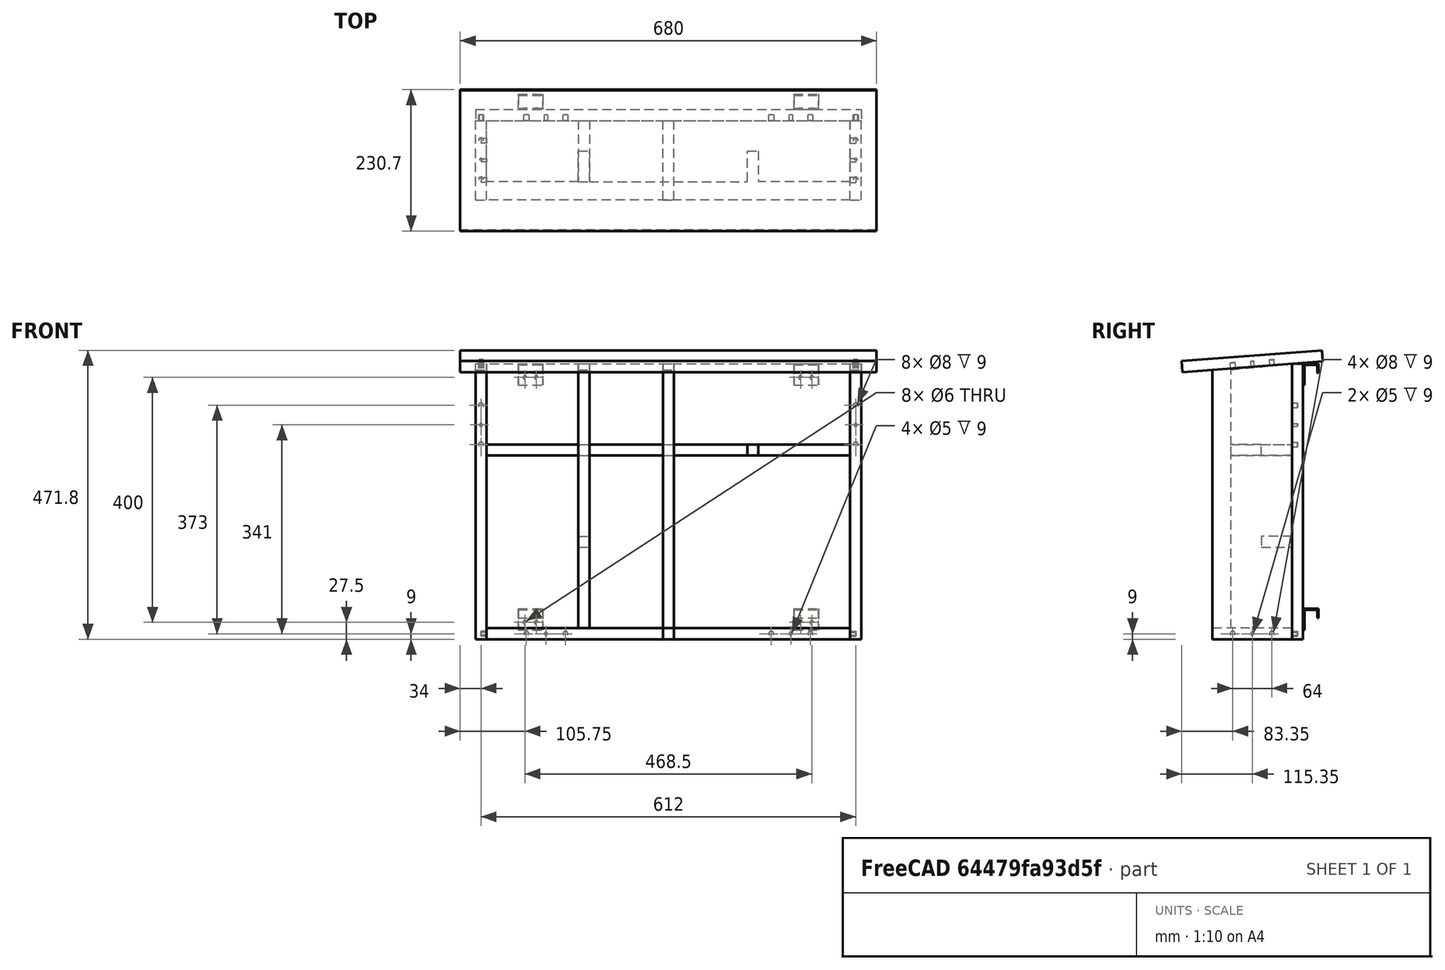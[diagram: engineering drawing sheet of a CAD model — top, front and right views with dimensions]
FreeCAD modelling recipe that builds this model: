
FCSTD DOCUMENT  (FreeCAD 0.19R24366 (Git))
Label: Insektenhotel
License: All rights reserved
LicenseURL: http://en.wikipedia.org/wiki/All_rights_reserved
objects: TechDraw::DrawViewDimension×47, PartDesign::Body×15, Sketcher::SketchObject×12, TechDraw::DrawProjGroupItem×10, PartDesign::FeatureBase×8, PartDesign::Pad×7, TechDraw::DrawSVGTemplate×7, TechDraw::DrawPage×7, TechDraw::DrawProjGroup×5, PartDesign::Pocket×4, App::DocumentObjectGroup×4, TechDraw::DrawViewPart×3, PartDesign::Hole×1
note: 59 computed .brp shape members not serialized (recipe doc carries the construction recipe); baked Part::Feature solids carry a one-line shape summary decoded from their .brp

FEATURE [Sketcher::SketchObject] Sketch
  FullyConstrained = true
  MapMode = 5
  Support = -> [XY_Plane,YZ_Plane,XZ_Plane]
  sketch-geometry (6):
    g0: LineSegment StartX=-340 StartY=115 StartZ=0 EndX=340 EndY=115 EndZ=0
    g1: LineSegment StartX=340 StartY=115 StartZ=0 EndX=340 EndY=-115 EndZ=0
    g2: LineSegment StartX=340 StartY=-115 StartZ=0 EndX=-340 EndY=-115 EndZ=0
    g3: LineSegment StartX=-340 StartY=-115 StartZ=0 EndX=-340 EndY=115 EndZ=0
    g4: LineSegment StartX=-340 StartY=0.0001 StartZ=0 EndX=340 EndY=0.0001 EndZ=0
    g5: LineSegment StartX=0 StartY=0 StartZ=0 EndX=0 EndY=0.0001 EndZ=0
  constraints (17):
    c: Coincident(g0,g1)
    c: Coincident(g1,g2)
    c: Coincident(g2,g3)
    c: Coincident(g3,g0)
    c: Horizontal(g2)
    c: Vertical(g3)
    c: DistanceX(g0,g0) = 680  'Länge'
    c: DistanceY(g2,g0) = 230  'Breite'
    c: Symmetric(g0,g0,g-2)
    c: Equal(g3,g1)
    c: PointOnObject(g4,g3)
    c: PointOnObject(g4,g1)
    c: Symmetric(g2,g0,g4)
    c: Coincident(g5,g-1)
    c: PointOnObject(g5,g4)
    c: Vertical(g5)
    c: DistanceY(g-1,g5) = 0.0001
FEATURE [PartDesign::Pad] Pad  label="Brett Dach"
  Direction = (1,1,1)
  Length = 18
  Length2 = 100
  Midplane = true
  Profile = -> Sketch
  Refine = true
  Type = 0
FEATURE [Sketcher::SketchObject] Sketch001
  FullyConstrained = true
  MapMode = 5
  Placement = pos=(0,0,0) rot=(0.57735,0.57735,0.57735;2.0944rad)
  Support = -> [YZ_Plane001]
  sketch-geometry (4):
    g0: LineSegment StartX=-65 StartY=440 StartZ=0 EndX=65 EndY=450 EndZ=0
    g1: LineSegment StartX=65 StartY=450 StartZ=0 EndX=65 EndY=0 EndZ=0
    g2: LineSegment StartX=65 StartY=0 StartZ=0 EndX=-65 EndY=0 EndZ=0
    g3: LineSegment StartX=-65 StartY=0 StartZ=0 EndX=-65 EndY=440 EndZ=0
  constraints (11):
    c: Coincident(g0,g1)
    c: Vertical(g1)
    c: Coincident(g1,g2)
    c: Coincident(g2,g3)
    c: Coincident(g3,g0)
    c: Vertical(g3)
    c: DistanceX(g2,g1) = 130
    c: DistanceY(g1,g0) = 450
    c: DistanceY(g3,g3) = 440
    c: Symmetric(g2,g1,g-2)
    c: PointOnObject(g1,g-1)
FEATURE [PartDesign::Pad] Pad001  label="Holz"
  Direction = (1,1,1)
  Length = 18
  Length2 = 100
  Midplane = true
  Placement = pos=(0,0,0) rot=(0.57735,0.57735,0.57735;2.0944rad)
  Profile = -> Sketch001
  Type = 0
FEATURE [PartDesign::Body] Body001  label="(Seite)"
  Group = -> [Sketch001,Pad001]
  Origin = -> Origin001
  Tip = -> Pad001
FEATURE [Sketcher::SketchObject] Sketch002
  FullyConstrained = true
  MapMode = 5
  Support = -> [XY_Plane002]
  sketch-geometry (4):
    g0: LineSegment StartX=-297 StartY=65 StartZ=0 EndX=297 EndY=65 EndZ=0
    g1: LineSegment StartX=297 StartY=65 StartZ=0 EndX=297 EndY=-65 EndZ=0
    g2: LineSegment StartX=297 StartY=-65 StartZ=0 EndX=-297 EndY=-65 EndZ=0
    g3: LineSegment StartX=-297 StartY=-65 StartZ=0 EndX=-297 EndY=65 EndZ=0
  constraints (10):
    c: Coincident(g0,g1)
    c: Coincident(g1,g2)
    c: Coincident(g2,g3)
    c: Coincident(g3,g0)
    c: Horizontal(g2)
    c: Vertical(g1)
    c: Symmetric(g0,g0,g-2)
    c: Symmetric(g0,g2,g-1)
    c: DistanceY(g3,g3) = 130  'Breite'
    c: DistanceX(g0,g0) = 594  'Länge'
FEATURE [PartDesign::Pad] Pad002
  Direction = (1,1,1)
  Length = 18
  Length2 = 100
  Profile = -> Sketch002
  Type = 0
FEATURE [PartDesign::Body] Body002  label="Boden"
  Group = -> [Sketch002,Pad002]
  Origin = -> Origin002
  Tip = -> Pad002
FEATURE [Sketcher::SketchObject] Sketch003
  FullyConstrained = true
  MapMode = 5
  Placement = pos=(0,0,0) rot=(1,0,0;1.5708rad)
  Support = -> [XZ_Plane003]
  sketch-geometry (4):
    g0: LineSegment StartX=-315 StartY=450 StartZ=0 EndX=315 EndY=450 EndZ=0
    g1: LineSegment StartX=315 StartY=450 StartZ=0 EndX=315 EndY=0 EndZ=0
    g2: LineSegment StartX=315 StartY=0 StartZ=0 EndX=-315 EndY=0 EndZ=0
    g3: LineSegment StartX=-315 StartY=0 StartZ=0 EndX=-315 EndY=450 EndZ=0
  constraints (11):
    c: Coincident(g0,g1)
    c: Coincident(g1,g2)
    c: Coincident(g2,g3)
    c: Coincident(g3,g0)
    c: Horizontal(g2)
    c: Vertical(g1)
    c: Vertical(g3)
    c: Symmetric(g0,g0,g-2)
    c: PointOnObject(g2,g-1)
    c: DistanceY(g3,g3) = 450
    c: DistanceX(g0,g0) = 630
FEATURE [PartDesign::Pad] Pad003  label="Brett Rückenwand"
  Direction = (1,1,1)
  Length = 18
  Length2 = 100
  Midplane = true
  Placement = pos=(0,0,0) rot=(1,0,0;1.5708rad)
  Profile = -> Sketch003
  Type = 0
FEATURE [PartDesign::FeatureBase] Clone006  label="Clone Seite L"
  BaseFeature = -> Pad001
  Placement = pos=(0,0,0) rot=(0.57735,0.57735,0.57735;2.0944rad)
FEATURE [Sketcher::SketchObject] Sketch007
  FullyConstrained = true
  MapMode = 5
  Placement = pos=(0,0,0) rot=(0.57735,0.57735,0.57735;2.0944rad)
  Support = -> [YZ_Plane006]
  sketch-geometry (4):
    g0: Circle CenterX=-32 CenterY=9 CenterZ=0 NormalX=0 NormalY=0 NormalZ=1 AngleXU=0 Radius=4
    g1: Circle CenterX=0 CenterY=9 CenterZ=0 NormalX=0 NormalY=0 NormalZ=1 AngleXU=0 Radius=2.5
    g2: Circle CenterX=32 CenterY=9 CenterZ=0 NormalX=0 NormalY=0 NormalZ=1 AngleXU=0 Radius=4
    g3: LineSegment StartX=-32 StartY=9 StartZ=0 EndX=32 EndY=9 EndZ=0
  constraints (10):
    c: Diameter(g0) = 8
    c: Equal(g0,g2)
    c: Diameter(g1) = 5
    c: Coincident(g3,g0)
    c: Coincident(g2,g3)
    c: DistanceX(g0,g2) = 64
    c: Symmetric(g0,g2,g-2)
    c: PointOnObject(g1,g3)
    c: PointOnObject(g1,g-2)
    c: DistanceY(g-1,g1) = 9
FEATURE [PartDesign::Pocket] Pocket001  label="Bohrloch Seite Links"
  BaseFeature = -> Clone006
  Length = 9
  Length2 = 100
  Placement = pos=(0,0,0) rot=(0.57735,0.57735,0.57735;2.0944rad)
  Profile = -> Sketch007
  Reversed = true
  Type = 0
FEATURE [PartDesign::Body] Body006  label="Seite Links"
  BaseFeature = -> Pad001
  Group = -> [Clone006,Sketch007,Pocket001]
  Origin = -> Origin006
  Placement = pos=(-306,0,0) rot=(0,0,1;0rad)
  Tip = -> Pocket001
FEATURE [PartDesign::FeatureBase] Clone  label="Clone Seite R"
  BaseFeature = -> Pad001
  Placement = pos=(0,0,0) rot=(0.57735,0.57735,0.57735;2.0944rad)
FEATURE [Sketcher::SketchObject] Sketch008
  FullyConstrained = true
  MapMode = 5
  Placement = pos=(0,0,0) rot=(0.57735,0.57735,0.57735;2.0944rad)
  Support = -> [YZ_Plane007]
  sketch-geometry (4):
    g0: Circle CenterX=-32 CenterY=9 CenterZ=0 NormalX=0 NormalY=0 NormalZ=1 AngleXU=0 Radius=4
    g1: Circle CenterX=0 CenterY=9 CenterZ=0 NormalX=0 NormalY=0 NormalZ=1 AngleXU=0 Radius=2.5
    g2: Circle CenterX=32 CenterY=9 CenterZ=0 NormalX=0 NormalY=0 NormalZ=1 AngleXU=0 Radius=4
    g3: LineSegment StartX=-32 StartY=9 StartZ=0 EndX=32 EndY=9 EndZ=0
  constraints (10):
    c: PointOnObject(g1,g-2)
    c: Diameter(g0) = 8
    c: Equal(g0,g2)
    c: Diameter(g1) = 5
    c: Coincident(g0,g3)
    c: Coincident(g2,g3)
    c: DistanceX(g3,g3) = 64
    c: Symmetric(g0,g2,g-2)
    c: PointOnObject(g1,g3)
    c: DistanceY(g-1,g1) = 9
FEATURE [PartDesign::Pocket] Pocket002  label="Bohrloch Seite Rechts"
  BaseFeature = -> Clone
  Length = 9
  Length2 = 100
  Placement = pos=(0,0,0) rot=(0.57735,0.57735,0.57735;2.0944rad)
  Profile = -> Sketch008
  Type = 0
FEATURE [PartDesign::Body] Body007  label="Seite Rechts"
  BaseFeature = -> Pad001
  Group = -> [Clone,Sketch008,Pocket002]
  Origin = -> Origin007
  Placement = pos=(306,0,0) rot=(0,0,1;0rad)
  Tip = -> Pocket002
FEATURE [Sketcher::SketchObject] Sketch009
  FullyConstrained = true
  MapMode = 5
  Support = -> [XY_Plane]
  sketch-geometry (7):
    g0: Circle CenterX=-306 CenterY=32 CenterZ=0 NormalX=0 NormalY=0 NormalZ=1 AngleXU=0 Radius=4
    g1: Circle CenterX=-306 CenterY=0 CenterZ=0 NormalX=0 NormalY=0 NormalZ=1 AngleXU=0 Radius=2.5
    g2: Circle CenterX=-306 CenterY=-32 CenterZ=0 NormalX=0 NormalY=0 NormalZ=1 AngleXU=0 Radius=4
    g3: LineSegment StartX=-306 StartY=32 StartZ=0 EndX=-306 EndY=-32 EndZ=0
    g4: Circle CenterX=306 CenterY=32 CenterZ=0 NormalX=0 NormalY=0 NormalZ=1 AngleXU=0 Radius=4
    g5: Circle CenterX=306 CenterY=-32 CenterZ=0 NormalX=0 NormalY=0 NormalZ=1 AngleXU=0 Radius=4
    g6: Circle CenterX=306 CenterY=0 CenterZ=0 NormalX=0 NormalY=0 NormalZ=1 AngleXU=0 Radius=2.5
  constraints (16):
    c: DistanceY(g3,g3) = 64
    c: Diameter(g0) = 8
    c: Equal(g0,g2)
    c: Diameter(g1) = 5
    c: Coincident(g0,g3)
    c: Coincident(g3,g2)
    c: Symmetric(g0,g2,g-1)
    c: PointOnObject(g1,g-1)
    c: PointOnObject(g1,g3)
    c: DistanceX(g1,g-1) = 306
    c: Equal(g0,g4)
    c: Equal(g0,g5)
    c: Equal(g1,g6)
    c: Symmetric(g0,g4,g-2)
    c: Symmetric(g2,g5,g-2)
    c: Symmetric(g1,g6,g-2)
FEATURE [PartDesign::Pocket] Pocket  label="Bohrloch Dach Links"
  BaseFeature = -> Pad
  Length = 9
  Length2 = 100
  Profile = -> Sketch009
  Type = 0
FEATURE [PartDesign::Body] Body  label="Dach"
  Group = -> [Sketch,Pad,Sketch009,Pocket]
  Origin = -> Origin
  Placement = pos=(0,0,454) rot=(1,0,0;0.076794rad)
  Tip = -> Pocket
FEATURE [Sketcher::SketchObject] Sketch010
  FullyConstrained = true
  MapMode = 5
  Placement = pos=(0,0,0) rot=(1,0,0;1.5708rad)
  Support = -> [XZ_Plane003]
  sketch-geometry (16):
    g0: Circle CenterX=-232 CenterY=9 CenterZ=0 NormalX=0 NormalY=0 NormalZ=1 AngleXU=0 Radius=4
    g1: Circle CenterX=-200 CenterY=9 CenterZ=0 NormalX=0 NormalY=0 NormalZ=1 AngleXU=0 Radius=2.5
    g2: Circle CenterX=-168 CenterY=9 CenterZ=0 NormalX=0 NormalY=0 NormalZ=1 AngleXU=0 Radius=4
    g3: Circle CenterX=168 CenterY=9 CenterZ=0 NormalX=0 NormalY=0 NormalZ=1 AngleXU=0 Radius=4
    g4: Circle CenterX=200 CenterY=9 CenterZ=0 NormalX=0 NormalY=0 NormalZ=1 AngleXU=0 Radius=2.5
    g5: Circle CenterX=232 CenterY=9 CenterZ=0 NormalX=0 NormalY=0 NormalZ=1 AngleXU=0 Radius=4
    g6: LineSegment StartX=168 StartY=9 StartZ=0 EndX=232 EndY=9 EndZ=0
    g7: LineSegment StartX=-168 StartY=9 StartZ=0 EndX=-232 EndY=9 EndZ=0
    g8: Circle CenterX=-306 CenterY=318 CenterZ=0 NormalX=0 NormalY=0 NormalZ=1 AngleXU=0 Radius=4
    g9: Circle CenterX=-306 CenterY=350 CenterZ=0 NormalX=0 NormalY=0 NormalZ=1 AngleXU=0 Radius=2.5
    g10: Circle CenterX=-306 CenterY=382 CenterZ=0 NormalX=0 NormalY=0 NormalZ=1 AngleXU=0 Radius=4
    g11: Circle CenterX=306 CenterY=382 CenterZ=0 NormalX=0 NormalY=0 NormalZ=1 AngleXU=0 Radius=4
    g12: Circle CenterX=306 CenterY=350 CenterZ=0 NormalX=0 NormalY=0 NormalZ=1 AngleXU=0 Radius=2.5
    g13: Circle CenterX=306 CenterY=318 CenterZ=0 NormalX=0 NormalY=0 NormalZ=1 AngleXU=0 Radius=4
    g14: LineSegment StartX=-306 StartY=382 StartZ=0 EndX=-306 EndY=318 EndZ=0
    g15: LineSegment StartX=306 StartY=382 StartZ=0 EndX=306 EndY=318 EndZ=0
  constraints (38):
    c: Diameter(g0) = 8
    c: Equal(g0,g2)
    c: Equal(g0,g3)
    c: Equal(g0,g5)
    c: Diameter(g1) = 5
    c: Equal(g1,g4)
    c: Horizontal(g6)
    c: Horizontal(g7)
    c: Coincident(g0,g7)
    c: Coincident(g2,g7)
    c: DistanceX(g7,g7) = 64
    c: Symmetric(g0,g2,g1)
    c: Coincident(g3,g6)
    c: Coincident(g6,g5)
    c: Symmetric(g3,g5,g4)
    c: Symmetric(g1,g4,g-2)
    c: DistanceX(g1,g4) = 400
    c: DistanceY(g3,g-1) = -9
    c: Equal(g0,g10)
    c: Equal(g0,g8)
    c: Equal(g0,g13)
    c: Equal(g0,g11)
    c: Equal(g1,g9)
    c: Equal(g1,g12)
    c: Vertical(g14)
    c: Vertical(g15)
    c: Coincident(g10,g14)
    c: Coincident(g8,g14)
    c: Coincident(g15,g13)
    c: Coincident(g15,g11)
    c: Symmetric(g11,g13,g12)
    c: Symmetric(g10,g8,g9)
    c: Equal(g7,g14)
    c: Equal(g7,g15)
    c: Equal(g7,g6)
    c: DistanceY(g-1,g9) = 350
    c: Symmetric(g9,g12,g-2)
    c: DistanceX(g9,g-1) = 306
FEATURE [PartDesign::Pocket] Pocket003  label="Bohrloch Rückenwand"
  BaseFeature = -> Pad003
  Length = 9
  Length2 = 100
  Placement = pos=(0,0,0) rot=(1,0,0;1.5708rad)
  Profile = -> Sketch010
  Reversed = true
  Type = 0
FEATURE [PartDesign::Body] Body003  label="Rückenwand"
  Group = -> [Sketch003,Pad003,Sketch010,Pocket003]
  Origin = -> Origin003
  Placement = pos=(0,74,0) rot=(0,0,1;0rad)
  Tip = -> Pocket003
FEATURE [TechDraw::DrawSVGTemplate] Template001
  Height = 210
  Orientation = 1
  Width = 297
FEATURE [App::DocumentObjectGroup] Gruppe  label="Gehäuse"
  Group = -> [Body,Body001,Body002,Body003,Body006,Body007]
FEATURE [TechDraw::DrawSVGTemplate] Template002
  Height = 210
  Orientation = 1
  Width = 297
FEATURE [TechDraw::DrawProjGroupItem] ProjItem  label="Front"
  CoarseView = false
  Direction = (0,-1,0)
  Focus = 100
  HardHidden = false
  IsoCount = 0
  IsoHidden = false
  IsoVisible = false
  LockPosition = true
  Perspective = false
  Rotation = 0
  RotationVector = (1,0,0)
  Scale = 0.3
  ScaleType = 2
  SeamHidden = false
  SeamVisible = true
  SmoothHidden = false
  SmoothVisible = true
  Source = -> [Body006]
  Type = 0
  X = 0
  XDirection = (1,0,0)
  Y = 0
FEATURE [TechDraw::DrawProjGroupItem] ProjItem002  label="Right"
  CoarseView = false
  Direction = (1,-1e-16,0)
  Focus = 100
  HardHidden = false
  IsoCount = 0
  IsoHidden = false
  IsoVisible = false
  LockPosition = false
  Perspective = false
  Rotation = 0
  RotationVector = (1,0,0)
  Scale = 0.3
  ScaleType = 2
  SeamHidden = false
  SeamVisible = true
  SmoothHidden = false
  SmoothVisible = true
  Source = -> [Body006]
  Type = 2
  X = -54
  XDirection = (1e-16,1,0)
  Y = 0
FEATURE [TechDraw::DrawProjGroup] ProjGroup
  Anchor = -> ProjItem
  AutoDistribute = true
  LockPosition = false
  ProjectionType = 0
  Rotation = 0
  Scale = 0.3
  ScaleType = 0
  Source = -> [Body006]
  Views = -> [ProjItem,ProjItem002]
  X = 120.774
  Y = 116.023
  spacingX = 15
  spacingY = 15
FEATURE [TechDraw::DrawViewDimension] Dimension011
  Arbitrary = false
  ArbitraryTolerances = false
  EqualTolerance = true
  FormatSpec = %.2f
  FormatSpecOverTolerance = %+.2f
  FormatSpecUnderTolerance = %+.2f
  Inverted = false
  LockPosition = false
  MeasureType = 1
  OverTolerance = 0
  References2D = -> [ProjItem002]
  Rotation = 0
  ScaleType = 0
  TheoreticalExact = false
  Type = 1
  UnderTolerance = 0
  X = -9.55524
  Y = -78.1164
FEATURE [TechDraw::DrawViewDimension] Dimension012
  Arbitrary = false
  ArbitraryTolerances = false
  EqualTolerance = true
  FormatSpec = %.2f
  FormatSpecOverTolerance = %+.2f
  FormatSpecUnderTolerance = %+.2f
  Inverted = false
  LockPosition = false
  MeasureType = 1
  OverTolerance = 0
  References2D = -> [ProjItem002]
  Rotation = 0
  ScaleType = 0
  TheoreticalExact = false
  Type = 2
  UnderTolerance = 0
  X = 33.11
  Y = -0.40619
FEATURE [TechDraw::DrawViewDimension] Dimension013
  Arbitrary = false
  ArbitraryTolerances = false
  EqualTolerance = true
  FormatSpec = %.2f
  FormatSpecOverTolerance = %+.2f
  FormatSpecUnderTolerance = %+.2f
  Inverted = false
  LockPosition = false
  MeasureType = 1
  OverTolerance = 0
  References2D = -> [ProjItem002]
  Rotation = 0
  ScaleType = 0
  TheoreticalExact = false
  Type = 2
  UnderTolerance = 0
  X = -30.8733
  Y = -1.90619
FEATURE [TechDraw::DrawViewDimension] Dimension014
  Arbitrary = false
  ArbitraryTolerances = false
  EqualTolerance = true
  FormatSpec = %.2f
  FormatSpecOverTolerance = %+.2f
  FormatSpecUnderTolerance = %+.2f
  Inverted = false
  LockPosition = false
  MeasureType = 1
  OverTolerance = 0
  References2D = -> [ProjItem]
  Rotation = 0
  ScaleType = 0
  TheoreticalExact = false
  Type = 1
  UnderTolerance = 0
  X = 0
  Y = -78.0609
FEATURE [TechDraw::DrawProjGroupItem] ProjItem003  label="Front001"
  CoarseView = false
  Direction = (0,-1,0)
  Focus = 100
  HardHidden = false
  IsoCount = 0
  IsoHidden = false
  IsoVisible = false
  LockPosition = true
  Perspective = false
  Rotation = 0
  RotationVector = (-1,0,0)
  Scale = 0.3
  ScaleType = 2
  SeamHidden = false
  SeamVisible = true
  SmoothHidden = false
  SmoothVisible = true
  Source = -> [Pocket]
  Type = 0
  X = 0
  XDirection = (-1,0,0)
  Y = 0
FEATURE [TechDraw::DrawProjGroupItem] ProjItem005  label="Top"
  CoarseView = false
  Direction = (0,0,-1)
  Focus = 100
  HardHidden = false
  IsoCount = 0
  IsoHidden = false
  IsoVisible = false
  LockPosition = false
  Perspective = false
  Rotation = 0
  RotationVector = (1,0,0)
  Scale = 0.3
  ScaleType = 2
  SeamHidden = false
  SeamVisible = true
  SmoothHidden = false
  SmoothVisible = true
  Source = -> [Pocket]
  Type = 4
  X = 0
  XDirection = (-1,0,0)
  Y = -84
FEATURE [TechDraw::DrawProjGroup] ProjGroup001
  Anchor = -> ProjItem003
  AutoDistribute = true
  LockPosition = false
  ProjectionType = 0
  Rotation = 0
  Scale = 0.3
  ScaleType = 2
  Source = -> [Pocket]
  Views = -> [ProjItem003,ProjItem005]
  X = 146.666
  Y = 175.034
  spacingX = 15
  spacingY = 15
FEATURE [TechDraw::DrawViewDimension] Dimension017
  Arbitrary = false
  ArbitraryTolerances = false
  EqualTolerance = true
  FormatSpec = %.2f
  FormatSpecOverTolerance = %+.2f
  FormatSpecUnderTolerance = %+.2f
  Inverted = false
  LockPosition = false
  MeasureType = 1
  OverTolerance = 0
  References2D = -> [ProjItem003]
  Rotation = 0
  ScaleType = 0
  TheoreticalExact = false
  Type = 2
  UnderTolerance = 0
  X = -125.777
  Y = 2.02312
FEATURE [TechDraw::DrawViewDimension] Dimension018
  Arbitrary = false
  ArbitraryTolerances = false
  EqualTolerance = true
  FormatSpec = %.2f
  FormatSpecOverTolerance = %+.2f
  FormatSpecUnderTolerance = %+.2f
  Inverted = false
  LockPosition = false
  MeasureType = 1
  OverTolerance = 0
  References2D = -> [ProjItem005]
  Rotation = 0
  ScaleType = 0
  TheoreticalExact = false
  Type = 2
  UnderTolerance = 0
  X = -60.1491
  Y = 17.0911
FEATURE [TechDraw::DrawSVGTemplate] Template
  Height = 210
  Orientation = 1
  Width = 297
FEATURE [TechDraw::DrawProjGroupItem] ProjItem006  label="Front002"
  CoarseView = false
  Direction = (0,-1,0)
  Focus = 100
  HardHidden = false
  IsoCount = 0
  IsoHidden = false
  IsoVisible = false
  LockPosition = true
  Perspective = false
  Rotation = 0
  RotationVector = (1,0,0)
  Scale = 0.25
  ScaleType = 2
  SeamHidden = false
  SeamVisible = true
  SmoothHidden = false
  SmoothVisible = true
  Source = -> [Body003]
  Type = 0
  X = 0
  XDirection = (1,0,0)
  Y = 0
FEATURE [TechDraw::DrawProjGroupItem] ProjItem008  label="Left"
  CoarseView = false
  Direction = (-1,-1e-16,0)
  Focus = 100
  HardHidden = false
  IsoCount = 0
  IsoHidden = false
  IsoVisible = false
  LockPosition = false
  Perspective = false
  Rotation = 0
  RotationVector = (1,0,0)
  Scale = 0.25
  ScaleType = 2
  SeamHidden = false
  SeamVisible = true
  SmoothHidden = false
  SmoothVisible = true
  Source = -> [Body003]
  Type = 1
  X = 96
  XDirection = (1e-16,-1,0)
  Y = 0
FEATURE [TechDraw::DrawProjGroup] ProjGroup002
  Anchor = -> ProjItem006
  AutoDistribute = true
  LockPosition = false
  ProjectionType = 0
  Rotation = 0
  Scale = 0.25
  ScaleType = 0
  Source = -> [Body003]
  Views = -> [ProjItem006,ProjItem008]
  X = 117.307
  Y = 105.175
  spacingX = 15
  spacingY = 15
FEATURE [TechDraw::DrawViewDimension] Dimension
  Arbitrary = false
  ArbitraryTolerances = false
  EqualTolerance = true
  FormatSpec = %.2f
  FormatSpecOverTolerance = %+.2f
  FormatSpecUnderTolerance = %+.2f
  Inverted = false
  LockPosition = false
  MeasureType = 1
  OverTolerance = 0
  References2D = -> [ProjItem008]
  Rotation = 0
  ScaleType = 0
  TheoreticalExact = false
  Type = 2
  UnderTolerance = 0
  X = 16.0604
  Y = -1.62476
FEATURE [TechDraw::DrawViewDimension] Dimension019
  Arbitrary = false
  ArbitraryTolerances = false
  EqualTolerance = true
  FormatSpec = %.2f
  FormatSpecOverTolerance = %+.2f
  FormatSpecUnderTolerance = %+.2f
  Inverted = false
  LockPosition = false
  MeasureType = 1
  OverTolerance = 0
  References2D = -> [ProjItem008]
  Rotation = 0
  ScaleType = 0
  TheoreticalExact = false
  Type = 1
  UnderTolerance = 0
  X = 0.812379
  Y = 65.5924
FEATURE [TechDraw::DrawViewDimension] Dimension020
  Arbitrary = false
  ArbitraryTolerances = false
  EqualTolerance = true
  FormatSpec = %.2f
  FormatSpecOverTolerance = %+.2f
  FormatSpecUnderTolerance = %+.2f
  Inverted = false
  LockPosition = false
  MeasureType = 1
  OverTolerance = 0
  References2D = -> [ProjItem006]
  Rotation = 0
  ScaleType = 0
  TheoreticalExact = false
  Type = 1
  UnderTolerance = 0
  X = 1.21857
  Y = 65.9985
FEATURE [TechDraw::DrawViewDimension] Dimension021
  Arbitrary = false
  ArbitraryTolerances = false
  EqualTolerance = true
  FormatSpec = %.2f
  FormatSpecOverTolerance = %+.2f
  FormatSpecUnderTolerance = %+.2f
  Inverted = false
  LockPosition = false
  MeasureType = 1
  OverTolerance = 0
  References2D = -> [ProjItem006]
  Rotation = 0
  ScaleType = 0
  TheoreticalExact = false
  Type = 2
  UnderTolerance = 0
  X = -92.5941
  Y = -14.8328
FEATURE [TechDraw::DrawViewDimension] Dimension022
  Arbitrary = false
  ArbitraryTolerances = false
  EqualTolerance = true
  FormatSpec = %.2f
  FormatSpecOverTolerance = %+.2f
  FormatSpecUnderTolerance = %+.2f
  Inverted = false
  LockPosition = false
  MeasureType = 1
  OverTolerance = 0
  References2D = -> [ProjItem006]
  Rotation = 0
  ScaleType = 0
  TheoreticalExact = false
  Type = 1
  UnderTolerance = 0
  X = -69.46
  Y = 51.915
FEATURE [TechDraw::DrawViewDimension] Dimension023
  Arbitrary = false
  ArbitraryTolerances = false
  EqualTolerance = true
  FormatSpec = %.2f
  FormatSpecOverTolerance = %+.2f
  FormatSpecUnderTolerance = %+.2f
  Inverted = false
  LockPosition = false
  MeasureType = 1
  OverTolerance = 0
  References2D = -> [ProjItem006]
  Rotation = 0
  ScaleType = 0
  TheoreticalExact = false
  Type = 1
  UnderTolerance = 0
  X = -60.5301
  Y = -60.038
FEATURE [TechDraw::DrawViewDimension] Dimension024
  Arbitrary = false
  ArbitraryTolerances = false
  EqualTolerance = true
  FormatSpec = %.2f
  FormatSpecOverTolerance = %+.2f
  FormatSpecUnderTolerance = %+.2f
  Inverted = false
  LockPosition = false
  MeasureType = 1
  OverTolerance = 0
  References2D = -> [ProjItem006]
  Rotation = 0
  ScaleType = 0
  TheoreticalExact = false
  Type = 2
  UnderTolerance = 0
  X = -34.8339
  Y = -45.9399
FEATURE [TechDraw::DrawViewDimension] Dimension025
  Arbitrary = false
  ArbitraryTolerances = false
  EqualTolerance = true
  FormatSpec = %.2f
  FormatSpecOverTolerance = %+.2f
  FormatSpecUnderTolerance = %+.2f
  Inverted = false
  LockPosition = false
  MeasureType = 1
  OverTolerance = 0
  References2D = -> [ProjItem006]
  Rotation = 0
  ScaleType = 0
  TheoreticalExact = false
  Type = 2
  UnderTolerance = 0
  X = 30.5618
  Y = -46.1535
FEATURE [TechDraw::DrawViewDimension] Dimension026
  Arbitrary = false
  ArbitraryTolerances = false
  EqualTolerance = true
  FormatSpec = %.2f
  FormatSpecOverTolerance = %+.2f
  FormatSpecUnderTolerance = %+.2f
  Inverted = false
  LockPosition = false
  MeasureType = 1
  OverTolerance = 0
  References2D = -> [ProjItem006]
  Rotation = 0
  ScaleType = 0
  TheoreticalExact = false
  Type = 1
  UnderTolerance = 0
  X = 65.0158
  Y = -60.2516
FEATURE [TechDraw::DrawViewDimension] Dimension027
  Arbitrary = false
  ArbitraryTolerances = false
  EqualTolerance = true
  FormatSpec = %.2f
  FormatSpecOverTolerance = %+.2f
  FormatSpecUnderTolerance = %+.2f
  Inverted = false
  LockPosition = false
  MeasureType = 1
  OverTolerance = 0
  References2D = -> [ProjItem006]
  Rotation = 0
  ScaleType = 0
  TheoreticalExact = false
  Type = 1
  UnderTolerance = 0
  X = 72.4436
  Y = 51.0613
FEATURE [TechDraw::DrawViewDimension] Dimension028
  Arbitrary = false
  ArbitraryTolerances = false
  EqualTolerance = true
  FormatSpec = %.2f
  FormatSpecOverTolerance = %+.2f
  FormatSpecUnderTolerance = %+.2f
  Inverted = false
  LockPosition = false
  MeasureType = 1
  OverTolerance = 0
  References2D = -> [ProjItem006]
  Rotation = 0
  ScaleType = 0
  TheoreticalExact = false
  Type = 2
  UnderTolerance = 0
  X = 85.5495
  Y = -12.8048
FEATURE [TechDraw::DrawPage] Page  label="Druck Rückenwand"
  KeepUpdated = true
  NextBalloonIndex = 1
  ProjectionType = 0
  Template = -> Template
  Views = -> [ProjGroup002,Dimension,Dimension019,Dimension020,Dimension021,Dimension022,Dimension023,Dimension024,Dimension025,Dimension026,Dimension027,Dimension028]
FEATURE [TechDraw::DrawViewDimension] Dimension029
  Arbitrary = false
  ArbitraryTolerances = false
  EqualTolerance = true
  FormatSpec = %.2f
  FormatSpecOverTolerance = %+.2f
  FormatSpecUnderTolerance = %+.2f
  Inverted = false
  LockPosition = false
  MeasureType = 1
  OverTolerance = 0
  References2D = -> [ProjItem002]
  Rotation = 0
  ScaleType = 0
  TheoreticalExact = false
  Type = 2
  UnderTolerance = 0
  X = 26.2119
  Y = -73.1602
FEATURE [TechDraw::DrawViewDimension] Dimension030
  Arbitrary = false
  ArbitraryTolerances = false
  EqualTolerance = true
  FormatSpec = %.2f
  FormatSpecOverTolerance = %+.2f
  FormatSpecUnderTolerance = %+.2f
  Inverted = false
  LockPosition = false
  MeasureType = 1
  OverTolerance = 0
  References2D = -> [ProjItem002]
  Rotation = 0
  ScaleType = 0
  TheoreticalExact = false
  Type = 1
  UnderTolerance = 0
  X = 1.52395
  Y = -89.7496
FEATURE [TechDraw::DrawProjGroupItem] ProjItem009  label="Front003"
  CoarseView = false
  Direction = (0,-1,0)
  Focus = 100
  HardHidden = false
  IsoCount = 0
  IsoHidden = false
  IsoVisible = false
  LockPosition = true
  Perspective = false
  Rotation = 0
  RotationVector = (1,0,0)
  Scale = 0.4
  ScaleType = 2
  SeamHidden = false
  SeamVisible = true
  SmoothHidden = false
  SmoothVisible = true
  Source = -> [Body002]
  Type = 0
  X = 0
  XDirection = (1,0,0)
  Y = 0
FEATURE [TechDraw::DrawProjGroupItem] ProjItem010  label="Bottom001"
  CoarseView = false
  Direction = (0,0,-1)
  Focus = 100
  HardHidden = false
  IsoCount = 0
  IsoHidden = false
  IsoVisible = false
  LockPosition = false
  Perspective = false
  Rotation = 0
  RotationVector = (1,0,0)
  Scale = 0.4
  ScaleType = 2
  SeamHidden = false
  SeamVisible = true
  SmoothHidden = false
  SmoothVisible = true
  Source = -> [Body002]
  Type = 5
  X = 0
  XDirection = (1,0,0)
  Y = 67
FEATURE [TechDraw::DrawProjGroup] ProjGroup003
  Anchor = -> ProjItem009
  AutoDistribute = true
  LockPosition = false
  ProjectionType = 0
  Rotation = 0
  Scale = 0.4
  ScaleType = 0
  Source = -> [Body002]
  Views = -> [ProjItem009,ProjItem010]
  X = 150.118
  Y = 62.1098
  spacingX = 15
  spacingY = 15
FEATURE [TechDraw::DrawViewDimension] Dimension031
  Arbitrary = false
  ArbitraryTolerances = false
  EqualTolerance = true
  FormatSpec = %.2f
  FormatSpecOverTolerance = %+.2f
  FormatSpecUnderTolerance = %+.2f
  Inverted = false
  LockPosition = false
  MeasureType = 1
  OverTolerance = 0
  References2D = -> [ProjItem009]
  Rotation = 0
  ScaleType = 0
  TheoreticalExact = false
  Type = 2
  UnderTolerance = 0
  X = -130.939
  Y = -1.21387
FEATURE [TechDraw::DrawViewDimension] Dimension032
  Arbitrary = false
  ArbitraryTolerances = false
  EqualTolerance = true
  FormatSpec = %.2f
  FormatSpecOverTolerance = %+.2f
  FormatSpecUnderTolerance = %+.2f
  Inverted = false
  LockPosition = false
  MeasureType = 1
  OverTolerance = 0
  References2D = -> [ProjItem010]
  Rotation = 0
  ScaleType = 0
  TheoreticalExact = false
  Type = 2
  UnderTolerance = 0
  X = -131.748
  Y = -0.809249
FEATURE [TechDraw::DrawViewDimension] Dimension033
  Arbitrary = false
  ArbitraryTolerances = false
  EqualTolerance = true
  FormatSpec = %.2f
  FormatSpecOverTolerance = %+.2f
  FormatSpecUnderTolerance = %+.2f
  Inverted = false
  LockPosition = false
  MeasureType = 1
  OverTolerance = 0
  References2D = -> [ProjItem010]
  Rotation = 0
  ScaleType = 0
  TheoreticalExact = false
  Type = 1
  UnderTolerance = 0
  X = 2.42775
  Y = 42.9942
FEATURE [TechDraw::DrawPage] Page001  label="Druck Boden"
  KeepUpdated = true
  NextBalloonIndex = 1
  ProjectionType = 0
  Template = -> Template001
  Views = -> [ProjGroup003,Dimension031,Dimension032,Dimension033]
FEATURE [TechDraw::DrawProjGroupItem] ProjItem011  label="Front004"
  CoarseView = false
  Direction = (0,-1,0)
  Focus = 100
  HardHidden = false
  IsoCount = 0
  IsoHidden = false
  IsoVisible = false
  LockPosition = true
  Perspective = false
  Rotation = 0
  RotationVector = (1,0,0)
  Scale = 0.3
  ScaleType = 2
  SeamHidden = false
  SeamVisible = true
  SmoothHidden = false
  SmoothVisible = true
  Source = -> [Body007]
  Type = 0
  X = 0
  XDirection = (1,0,0)
  Y = 0
FEATURE [TechDraw::DrawProjGroupItem] ProjItem012  label="Left001"
  CoarseView = false
  Direction = (-1,-1e-16,0)
  Focus = 100
  HardHidden = false
  IsoCount = 0
  IsoHidden = false
  IsoVisible = false
  LockPosition = false
  Perspective = false
  Rotation = 0
  RotationVector = (1,0,0)
  Scale = 0.3
  ScaleType = 2
  SeamHidden = false
  SeamVisible = true
  SmoothHidden = false
  SmoothVisible = true
  Source = -> [Body007]
  Type = 1
  X = 54
  XDirection = (1e-16,-1,0)
  Y = 0
FEATURE [TechDraw::DrawProjGroup] ProjGroup004
  Anchor = -> ProjItem011
  AutoDistribute = true
  LockPosition = false
  ProjectionType = 0
  Rotation = 0
  Scale = 0.3
  ScaleType = 0
  Source = -> [Body007]
  Views = -> [ProjItem011,ProjItem012]
  X = 191.122
  Y = 115.655
  spacingX = 15
  spacingY = 15
FEATURE [TechDraw::DrawPage] Page002  label="Druck Seite"
  KeepUpdated = true
  NextBalloonIndex = 1
  ProjectionType = 0
  Template = -> Template002
  Views = -> [ProjGroup,Dimension011,Dimension012,Dimension013,Dimension014,Dimension029,Dimension030,ProjGroup004]
FEATURE [TechDraw::DrawViewDimension] Dimension034
  Arbitrary = false
  ArbitraryTolerances = false
  EqualTolerance = true
  FormatSpec = %.2f
  FormatSpecOverTolerance = %+.2f
  FormatSpecUnderTolerance = %+.2f
  Inverted = false
  LockPosition = false
  MeasureType = 1
  OverTolerance = 0
  References2D = -> [ProjItem005]
  Rotation = 0
  ScaleType = 0
  TheoreticalExact = false
  Type = 1
  UnderTolerance = 0
  X = -1.17038
  Y = 65.6078
FEATURE [TechDraw::DrawViewDimension] Dimension035
  Arbitrary = false
  ArbitraryTolerances = false
  EqualTolerance = true
  FormatSpec = %.2f
  FormatSpecOverTolerance = %+.2f
  FormatSpecUnderTolerance = %+.2f
  Inverted = false
  LockPosition = false
  MeasureType = 1
  OverTolerance = 0
  References2D = -> [ProjItem005]
  Rotation = 0
  ScaleType = 0
  TheoreticalExact = false
  Type = 2
  UnderTolerance = 0
  X = -123.428
  Y = 3.64162
FEATURE [TechDraw::DrawSVGTemplate] Template003
  Height = 210
  Orientation = 1
  Width = 297
FEATURE [TechDraw::DrawSVGTemplate] Template004
  Height = 210
  Orientation = 1
  Width = 297
FEATURE [TechDraw::DrawViewDimension] Dimension036
  Arbitrary = false
  ArbitraryTolerances = false
  EqualTolerance = true
  FormatSpec = %.2f
  FormatSpecOverTolerance = %+.2f
  FormatSpecUnderTolerance = %+.2f
  Inverted = false
  LockPosition = false
  MeasureType = 1
  OverTolerance = 0
  References2D = -> [ProjItem005]
  Rotation = 0
  ScaleType = 0
  TheoreticalExact = false
  Type = 1
  UnderTolerance = 0
  X = -81.4974
  Y = 52.9275
FEATURE [TechDraw::DrawPage] Page003  label="Druck Dach"
  KeepUpdated = true
  NextBalloonIndex = 1
  ProjectionType = 0
  Template = -> Template003
  Views = -> [ProjGroup001,Dimension017,Dimension018,Dimension034,Dimension035,Dimension036]
FEATURE [Sketcher::SketchObject] Sketch013  label="Zaunhaken Loch"
  FullyConstrained = true
  MapMode = 5
  Placement = pos=(0,0,0) rot=(1,0,0;1.5708rad)
  Support = -> [XZ_Plane009]
  sketch-geometry (2):
    g0: Circle CenterX=-9.25 CenterY=-22.5 CenterZ=0 NormalX=0 NormalY=0 NormalZ=1 AngleXU=0 Radius=2.5
    g1: Circle CenterX=9.25 CenterY=-22.5 CenterZ=0 NormalX=0 NormalY=0 NormalZ=1 AngleXU=0 Radius=2.5
  constraints (5):
    c: Diameter(g0) = 5
    c: Equal(g0,g1)
    c: DistanceX(g0,g1) = 18.5
    c: Symmetric(g0,g1,g-2)
    c: DistanceY(g0,g-1) = 22.5
FEATURE [Sketcher::SketchObject] Sketch014  label="Zaunhaken Platte"
  FullyConstrained = true
  MapMode = 5
  Placement = pos=(0,0,0) rot=(0.57735,0.57735,0.57735;2.0944rad)
  Support = -> [YZ_Plane009]
  sketch-geometry (9):
    g0: LineSegment StartX=0 StartY=-35 StartZ=0 EndX=0 EndY=0 EndZ=0
    g1: LineSegment StartX=0 StartY=0 StartZ=0 EndX=25 EndY=0 EndZ=0
    g2: LineSegment StartX=25 StartY=0 StartZ=0 EndX=25 EndY=-15 EndZ=0
    g3: LineSegment StartX=25 StartY=-15 StartZ=0 EndX=23 EndY=-15 EndZ=0
    g4: LineSegment StartX=23 StartY=-15 StartZ=0 EndX=23 EndY=-2 EndZ=0
    g5: LineSegment StartX=23 StartY=-2 StartZ=0 EndX=2 EndY=-2 EndZ=0
    g6: LineSegment StartX=2 StartY=-2 StartZ=0 EndX=2 EndY=-35 EndZ=0
    g7: LineSegment StartX=2 StartY=-35 StartZ=0 EndX=0 EndY=-35 EndZ=0
    g8: LineSegment StartX=2 StartY=-2 StartZ=0 EndX=2 EndY=0 EndZ=0
  constraints (26):
    c: Vertical(g0)
    c: Coincident(g0,g1)
    c: Horizontal(g1)
    c: Coincident(g1,g2)
    c: Vertical(g2)
    c: Coincident(g2,g3)
    c: Horizontal(g3)
    c: Coincident(g3,g4)
    c: Vertical(g4)
    c: Coincident(g4,g5)
    c: Horizontal(g5)
    c: Coincident(g5,g6)
    c: Vertical(g6)
    c: Coincident(g6,g7)
    c: Coincident(g7,g0)
    c: Horizontal(g7)
    c: DistanceX(g7,g7) = 2
    c: Coincident(g8,g5)
    c: PointOnObject(g8,g1)
    c: Vertical(g8)
    c: Equal(g7,g8)
    c: DistanceX(g1,g1) = 25
    c: DistanceY(g0,g0) = 35
    c: Coincident(g0,g-1)
    c: DistanceY(g2,g2) = 15
    c: Equal(g7,g3)
FEATURE [PartDesign::Pad] Pad004
  Direction = (1,1,1)
  Length = 40
  Length2 = 100
  Midplane = true
  Placement = pos=(0,0,0) rot=(0.57735,0.57735,0.57735;2.0944rad)
  Profile = -> Sketch014
  Type = 0
FEATURE [PartDesign::Hole] Hole
  BaseFeature = -> Pad004
  Depth = 25
  DepthType = 0
  Diameter = 6
  DrillForDepth = false
  DrillPoint = 1
  DrillPointAngle = 118
  HoleCutCountersinkAngle = 90
  HoleCutCustomValues = false
  HoleCutDepth = 0
  HoleCutDiameter = 6.1
  HoleCutType = 0
  ModelActualThread = false
  Placement = pos=(0,0,0) rot=(0.57735,0.57735,0.57735;2.0944rad)
  Profile = -> Sketch013
  Tapered = false
  TaperedAngle = 90
  ThreadAngle = 0
  ThreadClass = 0
  ThreadCutOffInner = 0
  ThreadCutOffOuter = 0
  ThreadDirection = 0
  ThreadFit = 0
  ThreadPitch = 0
  ThreadSize = 0
  ThreadType = 0
  Threaded = false
FEATURE [PartDesign::Body] Body009  label="(Zaunhaken)"
  Group = -> [Sketch013,Sketch014,Pad004,Hole]
  Origin = -> Origin009
  Placement = pos=(0,83,0) rot=(0,0,1;0rad)
  Tip = -> Hole
FEATURE [PartDesign::FeatureBase] Clone007  label="Body Zaunhaken Oben / Links"
  BaseFeature = -> Body009
FEATURE [PartDesign::Body] Body010  label="Zaunhaken Oben / Rechts"
  BaseFeature = -> Body009
  Group = -> [Clone007]
  Origin = -> Origin010
  Placement = pos=(225,83,450) rot=(0,0,1;0rad)
  Tip = -> Clone007
FEATURE [PartDesign::FeatureBase] Clone008
  BaseFeature = -> Body009
FEATURE [PartDesign::Body] Body011  label="Zaunhaken Oben / Links"
  BaseFeature = -> Body009
  Group = -> [Clone008]
  Origin = -> Origin011
  Placement = pos=(-225,83,450) rot=(0,0,1;0rad)
  Tip = -> Clone008
FEATURE [PartDesign::FeatureBase] Clone009
  BaseFeature = -> Body009
FEATURE [PartDesign::Body] Body012  label="Zaunhaken Unten / Links"
  BaseFeature = -> Body009
  Group = -> [Clone009]
  Origin = -> Origin012
  Placement = pos=(225,83,50) rot=(0,0,1;0rad)
  Tip = -> Clone009
FEATURE [PartDesign::FeatureBase] Clone010
  BaseFeature = -> Body009
FEATURE [PartDesign::Body] Body013  label="Zaunhaken Unten / Rechts"
  BaseFeature = -> Body009
  Group = -> [Clone010]
  Origin = -> Origin013
  Placement = pos=(-225,83,50) rot=(0,0,1;0rad)
  Tip = -> Clone010
FEATURE [App::DocumentObjectGroup] Gruppe002  label="Gehäuse Befestigung"
  Group = -> [Body009,Body010,Body011,Body012,Body013]
FEATURE [TechDraw::DrawViewPart] View
  CoarseView = false
  Direction = (0,1,0)
  Focus = 100
  HardHidden = false
  IsoCount = 0
  IsoHidden = false
  IsoVisible = false
  LockPosition = false
  Perspective = false
  Rotation = 0
  Scale = 0.4
  ScaleType = 0
  SeamHidden = false
  SeamVisible = true
  SmoothHidden = false
  SmoothVisible = true
  Source = -> [Body003,Gruppe002]
  X = 162.48
  XDirection = (-1,0,0)
  Y = 101.353
FEATURE [TechDraw::DrawViewDimension] Dimension037
  Arbitrary = false
  ArbitraryTolerances = false
  EqualTolerance = true
  FormatSpec = %.2f
  FormatSpecOverTolerance = %+.2f
  FormatSpecUnderTolerance = %+.2f
  Inverted = false
  LockPosition = false
  MeasureType = 1
  OverTolerance = 0
  References2D = -> [View]
  Rotation = 0
  ScaleType = 0
  TheoreticalExact = false
  Type = 1
  UnderTolerance = 0
  X = -5.77424
  Y = 102.156
FEATURE [TechDraw::DrawViewDimension] Dimension038
  Arbitrary = false
  ArbitraryTolerances = false
  EqualTolerance = true
  FormatSpec = %.2f
  FormatSpecOverTolerance = %+.2f
  FormatSpecUnderTolerance = %+.2f
  Inverted = false
  LockPosition = false
  MeasureType = 1
  OverTolerance = 0
  References2D = -> [View]
  Rotation = 0
  ScaleType = 0
  TheoreticalExact = false
  Type = 1
  UnderTolerance = 0
  X = -112
  Y = 102.156
FEATURE [TechDraw::DrawViewDimension] Dimension039
  Arbitrary = false
  ArbitraryTolerances = false
  EqualTolerance = true
  FormatSpec = %.2f
  FormatSpecOverTolerance = %+.2f
  FormatSpecUnderTolerance = %+.2f
  Inverted = false
  LockPosition = false
  MeasureType = 1
  OverTolerance = 0
  References2D = -> [View]
  Rotation = 0
  ScaleType = 0
  TheoreticalExact = false
  Type = 1
  UnderTolerance = 0
  X = 112
  Y = 102.46
FEATURE [TechDraw::DrawViewDimension] Dimension040
  Arbitrary = false
  ArbitraryTolerances = false
  EqualTolerance = true
  FormatSpec = %.2f
  FormatSpecOverTolerance = %+.2f
  FormatSpecUnderTolerance = %+.2f
  Inverted = false
  LockPosition = false
  MeasureType = 1
  OverTolerance = 0
  References2D = -> [View]
  Rotation = 0
  ScaleType = 0
  TheoreticalExact = false
  Type = 1
  UnderTolerance = 0
  X = -105.499
  Y = 71.5789
FEATURE [TechDraw::DrawViewDimension] Dimension041
  Arbitrary = false
  ArbitraryTolerances = false
  EqualTolerance = true
  FormatSpec = %.2f
  FormatSpecOverTolerance = %+.2f
  FormatSpecUnderTolerance = %+.2f
  Inverted = false
  LockPosition = false
  MeasureType = 1
  OverTolerance = 0
  References2D = -> [View]
  Rotation = 0
  ScaleType = 0
  TheoreticalExact = false
  Type = 2
  UnderTolerance = 0
  X = -138.093
  Y = 74.8632
FEATURE [TechDraw::DrawViewDimension] Dimension042
  Arbitrary = false
  ArbitraryTolerances = false
  EqualTolerance = true
  FormatSpec = %.2f
  FormatSpecOverTolerance = %+.2f
  FormatSpecUnderTolerance = %+.2f
  Inverted = false
  LockPosition = false
  MeasureType = 1
  OverTolerance = 0
  References2D = -> [View]
  Rotation = 0
  ScaleType = 0
  TheoreticalExact = false
  Type = 2
  UnderTolerance = 0
  X = -70.4515
  Y = 85.1274
FEATURE [TechDraw::DrawViewDimension] Dimension043
  Arbitrary = false
  ArbitraryTolerances = false
  EqualTolerance = true
  FormatSpec = %.2f
  FormatSpecOverTolerance = %+.2f
  FormatSpecUnderTolerance = %+.2f
  Inverted = false
  LockPosition = false
  MeasureType = 1
  OverTolerance = 0
  References2D = -> [View]
  Rotation = 0
  ScaleType = 0
  TheoreticalExact = false
  Type = 2
  UnderTolerance = 0
  X = -145.41
  Y = 13.0391
FEATURE [TechDraw::DrawViewDimension] Dimension045
  Arbitrary = false
  ArbitraryTolerances = false
  EqualTolerance = true
  FormatSpec = %.2f
  FormatSpecOverTolerance = %+.2f
  FormatSpecUnderTolerance = %+.2f
  Inverted = false
  LockPosition = false
  MeasureType = 1
  OverTolerance = 0
  References2D = -> [View]
  Rotation = 0
  ScaleType = 0
  TheoreticalExact = false
  Type = 2
  UnderTolerance = 0
  X = -63.4616
  Y = -77.2648
FEATURE [TechDraw::DrawViewDimension] Dimension046
  Arbitrary = false
  ArbitraryTolerances = false
  EqualTolerance = true
  FormatSpec = %.2f
  FormatSpecOverTolerance = %+.2f
  FormatSpecUnderTolerance = %+.2f
  Inverted = false
  LockPosition = false
  MeasureType = 1
  OverTolerance = 0
  References2D = -> [View]
  Rotation = 0
  ScaleType = 0
  TheoreticalExact = false
  Type = 2
  UnderTolerance = 0
  X = -71.3632
  Y = -76.0593
FEATURE [TechDraw::DrawPage] Page004  label="Druck Zaunbfestigung"
  KeepUpdated = true
  NextBalloonIndex = 1
  ProjectionType = 0
  Template = -> Template004
  Views = -> [View,Dimension037,Dimension038,Dimension039,Dimension040,Dimension041,Dimension042,Dimension043,Dimension045,Dimension046]
FEATURE [Sketcher::SketchObject] Sketch015
  FullyConstrained = true
  MapMode = 5
  Placement = pos=(0,0,0) rot=(0.57735,0.57735,0.57735;2.0944rad)
  Support = -> [YZ_Plane014]
  sketch-geometry (12):
    g0: LineSegment StartX=0 StartY=0 StartZ=0 EndX=-100 EndY=0 EndZ=0
    g1: LineSegment StartX=-100 StartY=0 StartZ=0 EndX=-100 EndY=422 EndZ=0
    g2: LineSegment StartX=-100 StartY=422 StartZ=0 EndX=0 EndY=432 EndZ=0
    g3: LineSegment StartX=0 StartY=432 StartZ=0 EndX=-6.81e-14 EndY=300 EndZ=0
    g4: LineSegment StartX=6.33e-14 StartY=150 StartZ=0 EndX=-50 EndY=150 EndZ=0
    g5: LineSegment StartX=-50 StartY=132 StartZ=0 EndX=5.68e-14 EndY=132 EndZ=0
    g6: LineSegment StartX=-50 StartY=150 StartZ=0 EndX=-50 EndY=132 EndZ=0
    g7: LineSegment StartX=5.68e-14 StartY=132 StartZ=0 EndX=0 EndY=0 EndZ=0
    g8: LineSegment StartX=-8.32e-14 StartY=282 StartZ=0 EndX=-50 EndY=282 EndZ=0
    g9: LineSegment StartX=-50 StartY=282 StartZ=0 EndX=-50 EndY=300 EndZ=0
    g10: LineSegment StartX=-50 StartY=300 StartZ=0 EndX=-7.11e-14 EndY=300 EndZ=0
    g11: LineSegment StartX=-8.32e-14 StartY=282 StartZ=0 EndX=6.33e-14 EndY=150 EndZ=0
  constraints (33):
    c: Coincident(g-1,g0)
    c: PointOnObject(g0,g-1)
    c: Coincident(g0,g1)
    c: Vertical(g1)
    c: Coincident(g1,g2)
    c: PointOnObject(g2,g-2)
    c: Coincident(g2,g3)
    c: Coincident(g7,g0)
    c: DistanceX(g0,g0) = 100
    c: DistanceY(g7,g3) = 432
    c: DistanceY(g1,g1) = 422
    c: Horizontal(g4)
    c: Horizontal(g5)
    c: Coincident(g6,g4)
    c: Coincident(g6,g5)
    c: Vertical(g6)
    c: DistanceY(g6,g6) = 18
    c: DistanceX(g4,g4) = 50
    c: Coincident(g11,g4)
    c: Coincident(g7,g5)
    c: Tangent(g3,g7)
    c: DistanceY(g7,g7) = 132
    c: Horizontal(g8)
    c: Coincident(g9,g8)
    c: Vertical(g9)
    c: Coincident(g10,g9)
    c: Horizontal(g10)
    c: Equal(g5,g8)
    c: Equal(g6,g9)
    c: Coincident(g3,g10)
    c: Coincident(g11,g8)
    c: Tangent(g3,g11)
    c: Equal(g7,g3)
FEATURE [PartDesign::Pad] Pad005
  Direction = (1,1,1)
  Length = 18
  Length2 = 100
  Midplane = true
  Placement = pos=(0,0,0) rot=(0.57735,0.57735,0.57735;2.0944rad)
  Profile = -> Sketch015
  Type = 0
FEATURE [PartDesign::Body] Body014  label="Innenteil Senkrecht"
  Group = -> [Sketch015,Pad005]
  Origin = -> Origin014
  Placement = pos=(138,65,18) rot=(0,0,1;0rad)
  Tip = -> Pad005
FEATURE [Sketcher::SketchObject] Sketch016
  FullyConstrained = true
  MapMode = 5
  Support = -> [XY_Plane015]
  sketch-geometry (12):
    g0: LineSegment StartX=-297 StartY=0 StartZ=0 EndX=297 EndY=0 EndZ=0
    g1: LineSegment StartX=297 StartY=0 StartZ=0 EndX=297 EndY=-100 EndZ=0
    g2: LineSegment StartX=297 StartY=-100 StartZ=0 EndX=147 EndY=-100 EndZ=0
    g3: LineSegment StartX=-297 StartY=-100 StartZ=0 EndX=-297 EndY=0 EndZ=0
    g4: LineSegment StartX=-147 StartY=-100 StartZ=0 EndX=-147 EndY=-50 EndZ=0
    g5: LineSegment StartX=147 StartY=-50 StartZ=0 EndX=147 EndY=-100 EndZ=0
    g6: LineSegment StartX=-147 StartY=-100 StartZ=0 EndX=-297 EndY=-100 EndZ=0
    g7: LineSegment StartX=-147 StartY=-50 StartZ=0 EndX=-129 EndY=-50 EndZ=0
    g8: LineSegment StartX=-129 StartY=-100 StartZ=0 EndX=-129 EndY=-50 EndZ=0
    g9: LineSegment StartX=129 StartY=-100 StartZ=0 EndX=129 EndY=-50 EndZ=0
    g10: LineSegment StartX=129 StartY=-50 StartZ=0 EndX=147 EndY=-50 EndZ=0
    g11: LineSegment StartX=-129 StartY=-100 StartZ=0 EndX=129 EndY=-100 EndZ=0
  constraints (33):
    c: PointOnObject(g0,g-1)
    c: Coincident(g0,g1)
    c: Vertical(g1)
    c: Coincident(g1,g2)
    c: Horizontal(g2)
    c: Coincident(g6,g3)
    c: Coincident(g3,g0)
    c: Vertical(g3)
    c: DistanceY(g3,g3) = 100
    c: DistanceX(g0,g0) = 594
    c: Symmetric(g0,g0,g-1)
    c: Vertical(g4)
    c: Vertical(g5)
    c: DistanceY(g4,g4) = 50
    c: Coincident(g6,g4)
    c: Tangent(g2,g6)
    c: Coincident(g2,g5)
    c: DistanceX(g6,g6) = 150
    c: Equal(g6,g2)
    c: Coincident(g10,g5)
    c: Horizontal(g7)
    c: Coincident(g7,g4)
    c: Vertical(g8)
    c: Vertical(g9)
    c: Coincident(g7,g8)
    c: Coincident(g10,g9)
    c: Tangent(g7,g10)
    c: DistanceX(g7,g7) = 18
    c: Equal(g7,g10)
    c: Equal(g4,g8)
    c: Equal(g4,g9)
    c: Coincident(g11,g8)
    c: Coincident(g11,g9)
FEATURE [PartDesign::Pad] Pad006
  Direction = (1,1,1)
  Length = 18
  Length2 = 100
  Midplane = true
  Profile = -> Sketch016
  Type = 0
FEATURE [PartDesign::Body] Body015  label="Innenteil Waagrecht"
  Group = -> [Sketch016,Pad006]
  Origin = -> Origin015
  Placement = pos=(0,65,159) rot=(0,0,1;0rad)
  Tip = -> Pad006
FEATURE [PartDesign::FeatureBase] Clone011
  BaseFeature = -> Body014
  Placement = pos=(92,0,0) rot=(0,0,1;0rad)
FEATURE [PartDesign::Body] Body016  label="Innenteil Senkrecht Links"
  BaseFeature = -> Body014
  Group = -> [Clone011]
  Origin = -> Origin016
  Placement = pos=(-230,65,18) rot=(0,0,1;0rad)
  Tip = -> Clone011
FEATURE [PartDesign::FeatureBase] Clone012
  BaseFeature = -> Body015
  Placement = pos=(0,0,142) rot=(0,0,1;0rad)
FEATURE [PartDesign::Body] Body017  label="Innenteil Waagrecht Oben"
  BaseFeature = -> Body015
  Group = -> [Clone012]
  Origin = -> Origin017
  Placement = pos=(0,65,167) rot=(0,0,1;0rad)
  Tip = -> Clone012
FEATURE [App::DocumentObjectGroup] Gruppe003  label="Gehäuse Innenteil"
  Group = -> [Body014,Body015,Body016,Body017]
FEATURE [TechDraw::DrawSVGTemplate] Template005
  Height = 210
  Orientation = 1
  Width = 297
FEATURE [TechDraw::DrawViewPart] View001
  CoarseView = false
  Direction = (0,0,1)
  Focus = 100
  HardHidden = false
  IsoCount = 0
  IsoHidden = false
  IsoVisible = false
  LockPosition = false
  Perspective = false
  Rotation = 0
  Scale = 0.3
  ScaleType = 0
  SeamHidden = false
  SeamVisible = true
  SmoothHidden = false
  SmoothVisible = true
  Source = -> [Clone012]
  X = 148.5
  XDirection = (1,0,0)
  Y = 105
FEATURE [TechDraw::DrawViewDimension] Dimension047
  Arbitrary = false
  ArbitraryTolerances = false
  EqualTolerance = true
  FormatSpec = %.2f
  FormatSpecOverTolerance = %+.2f
  FormatSpecUnderTolerance = %+.2f
  Inverted = false
  LockPosition = false
  MeasureType = 1
  OverTolerance = 0
  References2D = -> [View001]
  Rotation = 0
  Scale = 0.3
  ScaleType = 0
  TheoreticalExact = false
  Type = 2
  UnderTolerance = 0
  X = -118.579
  Y = -0.607815
FEATURE [TechDraw::DrawViewDimension] Dimension048
  Arbitrary = false
  ArbitraryTolerances = false
  EqualTolerance = true
  FormatSpec = %.2f
  FormatSpecOverTolerance = %+.2f
  FormatSpecUnderTolerance = %+.2f
  Inverted = false
  LockPosition = false
  MeasureType = 1
  OverTolerance = 0
  References2D = -> [View001]
  Rotation = 0
  Scale = 0.3
  ScaleType = 0
  TheoreticalExact = false
  Type = 1
  UnderTolerance = 0
  X = 0.607815
  Y = 34.1462
FEATURE [TechDraw::DrawViewDimension] Dimension049
  Arbitrary = false
  ArbitraryTolerances = false
  EqualTolerance = true
  FormatSpec = %.2f
  FormatSpecOverTolerance = %+.2f
  FormatSpecUnderTolerance = %+.2f
  Inverted = false
  LockPosition = false
  MeasureType = 1
  OverTolerance = 0
  References2D = -> [View001]
  Rotation = 0
  Scale = 0.3
  ScaleType = 0
  TheoreticalExact = false
  Type = 2
  UnderTolerance = 0
  X = -103.058
  Y = -4.76483
FEATURE [TechDraw::DrawViewDimension] Dimension050
  Arbitrary = false
  ArbitraryTolerances = false
  EqualTolerance = true
  FormatSpec = %.2f
  FormatSpecOverTolerance = %+.2f
  FormatSpecUnderTolerance = %+.2f
  Inverted = false
  LockPosition = false
  MeasureType = 1
  OverTolerance = 0
  References2D = -> [View001]
  Rotation = 0
  Scale = 0.3
  ScaleType = 0
  TheoreticalExact = false
  Type = 1
  UnderTolerance = 0
  X = -66.6
  Y = -22.9016
FEATURE [TechDraw::DrawViewDimension] Dimension051
  Arbitrary = false
  ArbitraryTolerances = false
  EqualTolerance = true
  FormatSpec = %.2f
  FormatSpecOverTolerance = %+.2f
  FormatSpecUnderTolerance = %+.2f
  Inverted = false
  LockPosition = false
  MeasureType = 1
  OverTolerance = 0
  References2D = -> [View001]
  Rotation = 0
  Scale = 0.3
  ScaleType = 0
  TheoreticalExact = false
  Type = 1
  UnderTolerance = 0
  X = 68.4234
  Y = -22.2938
FEATURE [TechDraw::DrawViewDimension] Dimension052
  Arbitrary = false
  ArbitraryTolerances = false
  EqualTolerance = true
  FormatSpec = %.2f
  FormatSpecOverTolerance = %+.2f
  FormatSpecUnderTolerance = %+.2f
  Inverted = false
  LockPosition = false
  MeasureType = 1
  OverTolerance = 0
  References2D = -> [View001]
  Rotation = 0
  Scale = 0.3
  ScaleType = 0
  TheoreticalExact = false
  Type = 1
  UnderTolerance = 0
  X = 29.2437
  Y = -22.1852
FEATURE [TechDraw::DrawPage] Page005  label="Druck Innen Waagrecht"
  KeepUpdated = true
  NextBalloonIndex = 1
  ProjectionType = 0
  Scale = 0.3
  Template = -> Template005
  Views = -> [View001,Dimension047,Dimension048,Dimension049,Dimension050,Dimension051,Dimension052]
FEATURE [TechDraw::DrawSVGTemplate] Template006
  Height = 210
  Orientation = 1
  Width = 297
FEATURE [TechDraw::DrawViewPart] View002
  CoarseView = false
  Direction = (1,0,0)
  Focus = 100
  HardHidden = false
  IsoCount = 0
  IsoHidden = false
  IsoVisible = false
  LockPosition = false
  Perspective = false
  Rotation = 0
  Scale = 0.3
  ScaleType = 0
  SeamHidden = false
  SeamVisible = true
  SmoothHidden = false
  SmoothVisible = true
  Source = -> [Body014]
  X = 143.03
  XDirection = (0,1,0)
  Y = 121.107
FEATURE [TechDraw::DrawViewDimension] Dimension053
  Arbitrary = false
  ArbitraryTolerances = false
  EqualTolerance = true
  FormatSpec = %.2f
  FormatSpecOverTolerance = %+.2f
  FormatSpecUnderTolerance = %+.2f
  Inverted = false
  LockPosition = false
  MeasureType = 1
  OverTolerance = 0
  References2D = -> [View002]
  Rotation = 0
  Scale = 0.3
  ScaleType = 0
  TheoreticalExact = false
  Type = 2
  UnderTolerance = 0
  X = -33.5384
  Y = -3.32344
FEATURE [TechDraw::DrawViewDimension] Dimension054
  Arbitrary = false
  ArbitraryTolerances = false
  EqualTolerance = true
  FormatSpec = %.2f
  FormatSpecOverTolerance = %+.2f
  FormatSpecUnderTolerance = %+.2f
  Inverted = false
  LockPosition = false
  MeasureType = 1
  OverTolerance = 0
  References2D = -> [View002]
  Rotation = 0
  Scale = 0.3
  ScaleType = 0
  TheoreticalExact = false
  Type = 2
  UnderTolerance = 0
  X = 45.0868
  Y = 0.911722
FEATURE [TechDraw::DrawViewDimension] Dimension055
  Arbitrary = false
  ArbitraryTolerances = false
  EqualTolerance = true
  FormatSpec = %.2f
  FormatSpecOverTolerance = %+.2f
  FormatSpecUnderTolerance = %+.2f
  Inverted = false
  LockPosition = false
  MeasureType = 1
  OverTolerance = 0
  References2D = -> [View002]
  Rotation = 0
  Scale = 0.3
  ScaleType = 0
  TheoreticalExact = false
  Type = 2
  UnderTolerance = 0
  X = 28.068
  Y = 43.7844
FEATURE [TechDraw::DrawViewDimension] Dimension056
  Arbitrary = false
  ArbitraryTolerances = false
  EqualTolerance = true
  FormatSpec = %.2f
  FormatSpecOverTolerance = %+.2f
  FormatSpecUnderTolerance = %+.2f
  Inverted = false
  LockPosition = false
  MeasureType = 1
  OverTolerance = 0
  References2D = -> [View002]
  Rotation = 0
  Scale = 0.3
  ScaleType = 0
  TheoreticalExact = false
  Type = 2
  UnderTolerance = 0
  X = 27.9595
  Y = 12.1671
FEATURE [TechDraw::DrawViewDimension] Dimension057
  Arbitrary = false
  ArbitraryTolerances = false
  EqualTolerance = true
  FormatSpec = %.2f
  FormatSpecOverTolerance = %+.2f
  FormatSpecUnderTolerance = %+.2f
  Inverted = false
  LockPosition = false
  MeasureType = 1
  OverTolerance = 0
  References2D = -> [View002]
  Rotation = 0
  Scale = 0.3
  ScaleType = 0
  TheoreticalExact = false
  Type = 2
  UnderTolerance = 0
  X = 27.1563
  Y = -46.2156
FEATURE [TechDraw::DrawViewDimension] Dimension058
  Arbitrary = false
  ArbitraryTolerances = false
  EqualTolerance = true
  FormatSpec = %.2f
  FormatSpecOverTolerance = %+.2f
  FormatSpecUnderTolerance = %+.2f
  Inverted = false
  LockPosition = false
  MeasureType = 1
  OverTolerance = 0
  References2D = -> [View002]
  Rotation = 0
  Scale = 0.3
  ScaleType = 0
  TheoreticalExact = false
  Type = 1
  UnderTolerance = 0
  X = 8.10782
  Y = -78.0799
FEATURE [TechDraw::DrawViewDimension] Dimension059
  Arbitrary = false
  ArbitraryTolerances = false
  EqualTolerance = true
  FormatSpec = %.2f
  FormatSpecOverTolerance = %+.2f
  FormatSpecUnderTolerance = %+.2f
  Inverted = false
  LockPosition = false
  MeasureType = 1
  OverTolerance = 0
  References2D = -> [View002]
  Rotation = 0
  Scale = 0.3
  ScaleType = 0
  TheoreticalExact = false
  Type = 1
  UnderTolerance = 0
  X = 0.607815
  Y = -91.2399
FEATURE [TechDraw::DrawPage] Page006  label="Druck Innen Senkrecht"
  KeepUpdated = true
  NextBalloonIndex = 1
  ProjectionType = 0
  Scale = 0.3
  Template = -> Template006
  Views = -> [View002,Dimension053,Dimension054,Dimension055,Dimension056,Dimension057,Dimension058,Dimension059]
FEATURE [App::DocumentObjectGroup] Gruppe001  label="Druck"
  Group = -> [Page002,Page001,Page003,Page,Page004,Page005,Page006]
